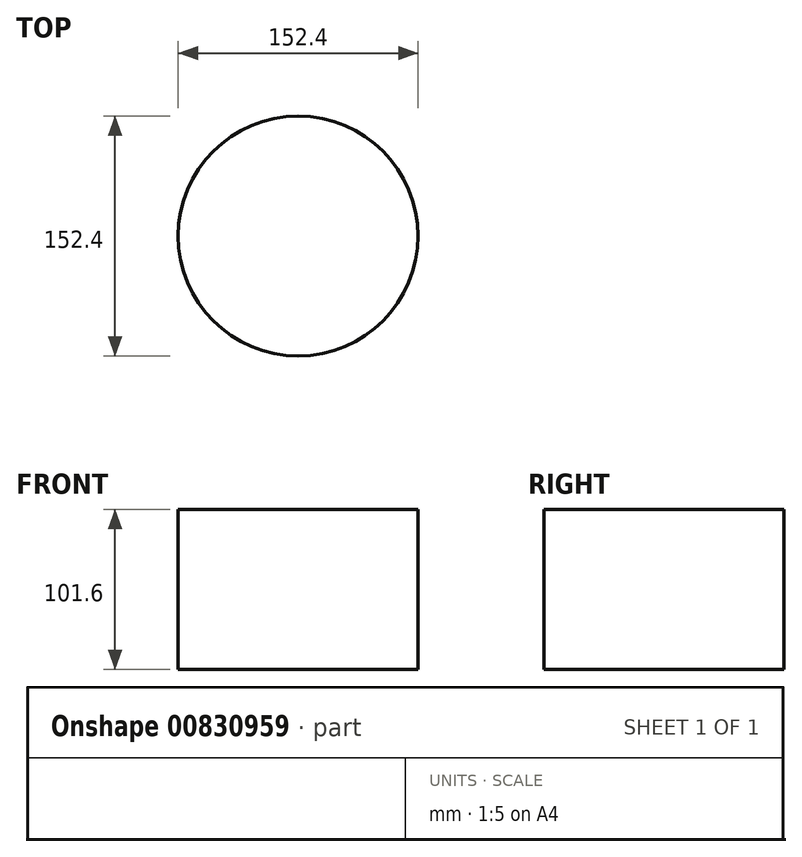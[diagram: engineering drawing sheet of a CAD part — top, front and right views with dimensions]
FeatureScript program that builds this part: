
annotation { "Feature Type Name" : "Feature", "Feature Type Description" : "" }
export const myFeature = defineFeature(function(context is Context, id is Id, definition is map)
    precondition{}
    {
        {
            var Q0;
            Q0=qCreatedBy(makeId("Top.planeOp"),FACE);
            var sketch = newSketch(context, id + "F0", { "sketchPlane" : qUnion([Q0])});
            skCircle(sketch, "E0", {"center": v(0, 0) * mm, "radius": 76.2 * mm});
            skSolve(sketch);
        }
        {
            var Q0;
            Q0 = qSketchRegion(id + "F0", true);
            extrude(context, id + "F1", {"entities" : qUnion([Q0]), "depth" : 101.6 * mm, "offsetDistance" : 25.4 * mm});
        }
    });
